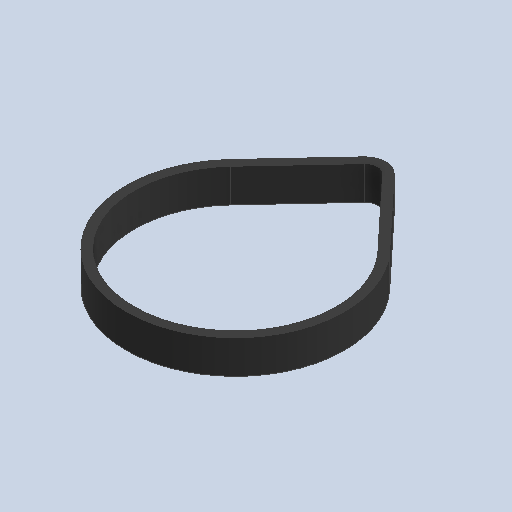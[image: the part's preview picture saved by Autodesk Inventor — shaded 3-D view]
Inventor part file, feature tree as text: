
AUTODESK INVENTOR PART (.ipt)
format: ipt  version: 2024 (Build 280153000, 153)  size: 90,624 bytes
history: native  units: in
note: dims shown in document units (in); Inventor stores cm internally (conversion verified against a paired STEP export)
features: extrude x1
ambient origin geometry x8: Origin, YZ Plane, XZ Plane, XY Plane, X Axis, Y Axis, Z Axis, Center Point
bodies: Solid1 (feature_tree)
feature tree (1):
  extrude  "Extrude-Thin1"  [1 undecoded]
note: 1 required parameter value undecoded (feature->parameter linkage not recoverable at this tier; creation-order binding heuristic only, values carry confidence <= 0.55)
